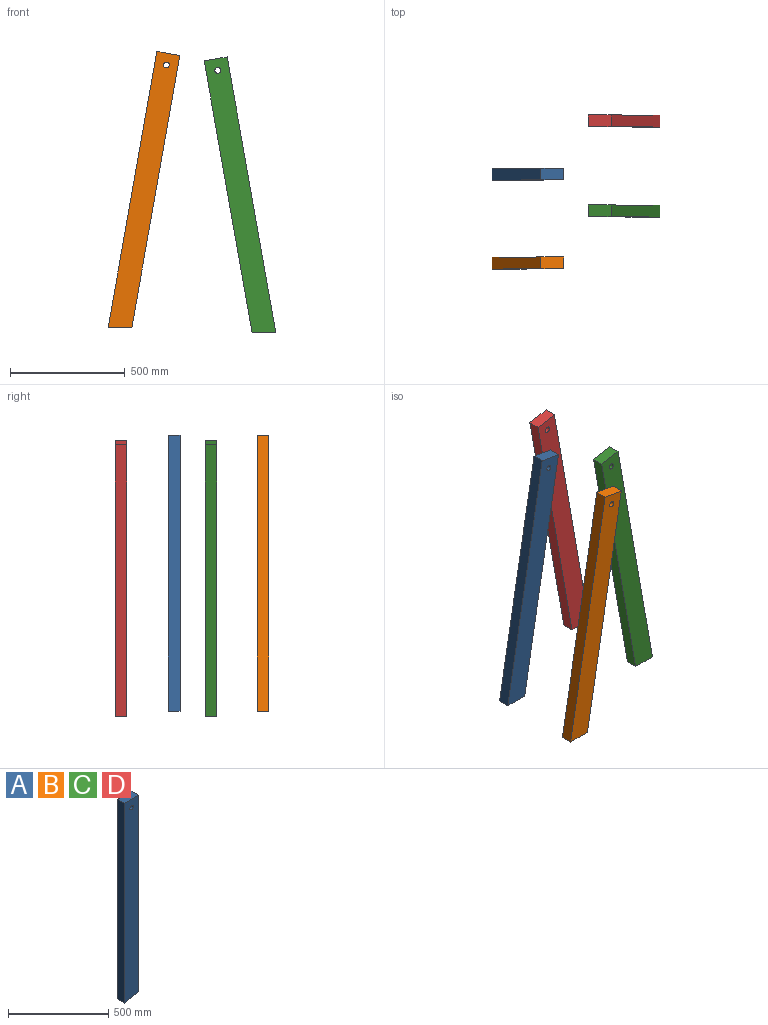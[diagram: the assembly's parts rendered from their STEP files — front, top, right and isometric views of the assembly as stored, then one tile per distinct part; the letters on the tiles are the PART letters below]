
ASSEMBLY  parts=4 mates=2
PART A: 7 faces, bbox 101.6x50.8x1219.2 mm
  f0: plane 1219.2x50.8mm, normal (-1,0,0), area 61935.4mm2, adj f1,f3,f4,f5
  f1: plane 101.6x50.8mm, normal (0.17,0,-0.98), area 5240.9mm2, adj f0,f2,f4,f5
  f2: plane 1201.29x50.8mm, normal (1,0,0), area 61025.3mm2, adj f1,f3,f4,f5
  f3: plane 101.6x50.8mm, normal (0,0,1), area 5161.3mm2, adj f0,f2,f4,f5
  f4: plane 1219.2x101.6mm, normal (0,-1,0), area 122453.9mm2, adj f0,f1,f2,f3,f6
  f5: plane 1219.2x101.6mm, normal (0,1,0), area 122453.9mm2, adj f0,f1,f2,f3,f6
  f6: cylinder r=12.7mm len=50.8mm, axis (0,-1,0), area 4053.7mm2, adj f4,f5
PART B: same geometry as A
PART C: same geometry as A
PART D: same geometry as A
PLACE A rot(axis=(0,1,0),10deg) t=(-1271.18,-51.69,-758.5)mm
PLACE B rot(axis=(0,1,0),10deg) t=(-1271.18,-438.5,-758.5)mm
PLACE C rot(axis=(-0.09,0,1),180deg) t=(-628.99,-262.81,-782.12)mm
PLACE D rot(axis=(-0.09,0,1),180deg) t=(-628.99,129.4,-782.12)mm
MATE cylindrical A.f6 <-> B.f6  axis (0,-1,0) through (-1062.01,-102.49,546.16)mm
MATE cylindrical D.f6 <-> C.f6  axis (0,-1,0) through (-838.16,129.4,522.54)mm
